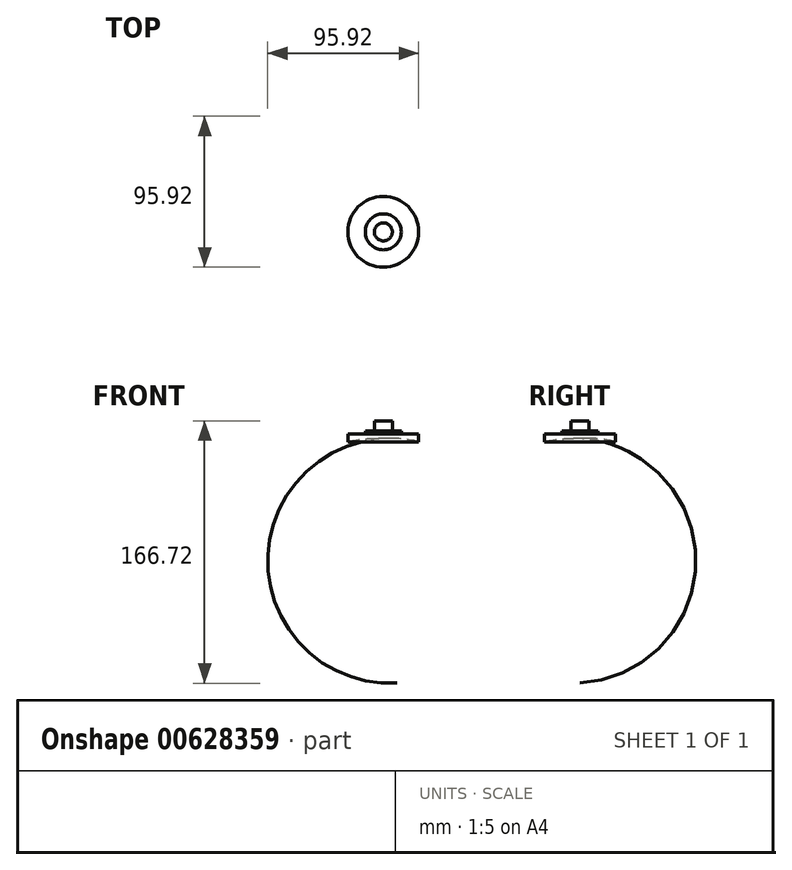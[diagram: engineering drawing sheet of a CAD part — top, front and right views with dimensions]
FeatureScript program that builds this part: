
annotation { "Feature Type Name" : "Feature", "Feature Type Description" : "" }
export const myFeature = defineFeature(function(context is Context, id is Id, definition is map)
    precondition{}
    {
        {
            var Q0;
            Q0=qCreatedBy(makeId("Front.planeOp"),FACE);
            var sketch = newSketch(context, id + "F0", { "sketchPlane" : qUnion([Q0])});
            skLineSegment(sketch, "E0.bottom", {"start": v(-22.5, 5) * mm, "end": v(-11.43, 5) * mm});
            skLineSegment(sketch, "E0.left", {"start": v(-22.5, 5) * mm, "end": v(-22.5, 0) * mm});
            skLineSegment(sketch, "E1.top", {"start": v(-11.43, 7) * mm, "end": v(-5.72, 7) * mm});
            skLineSegment(sketch, "E1.left", {"start": v(-11.43, 5) * mm, "end": v(-11.43, 7) * mm});
            skLineSegment(sketch, "E2.top", {"start": v(-5.72, 13.35) * mm, "end": v(0, 13.35) * mm});
            skLineSegment(sketch, "E2.left", {"start": v(-5.72, 7) * mm, "end": v(-5.72, 13.35) * mm});
            skLineSegment(sketch, "E3", {"start": v(0, 13.35) * mm, "end": v(0, 2.03) * mm});
            skArc(sketch, "E4", {"start": v(0, 2.03) * mm, "mid": v(-11.32, 1.84) * mm, "end": v(-22.5, 0) * mm});
            skSolve(sketch);
        }
        {
            var Q0;
            Q0 = qSketchRegion(id + "F0", true);
            var Q1;
            Q1=sQuery(id+"F0.wireOp",EDGE,"E3");
            revolve(context, id + "F1", {"entities" : qUnion([Q0]), "axis" : qUnion([Q1]), "revolveType" : RevolveType.FULL});
        }
    });
